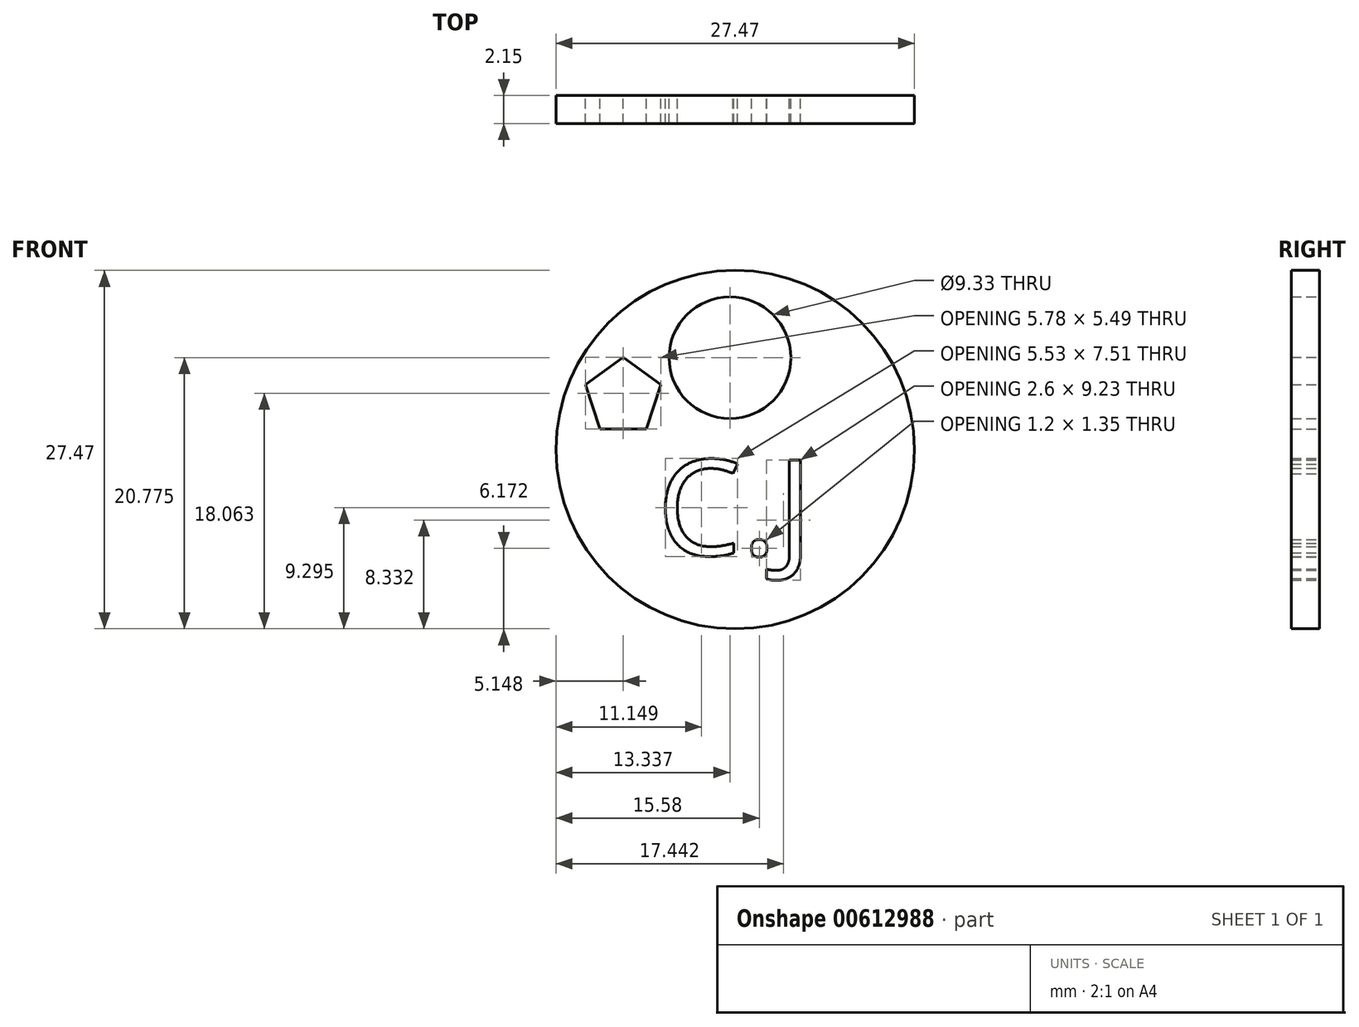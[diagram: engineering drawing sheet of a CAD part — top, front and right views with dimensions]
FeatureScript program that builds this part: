
annotation { "Feature Type Name" : "Feature", "Feature Type Description" : "" }
export const myFeature = defineFeature(function(context is Context, id is Id, definition is map)
    precondition{}
    {
        {
            var Q0;
            Q0=qCreatedBy(makeId("Front.planeOp"),FACE);
            var sketch = newSketch(context, id + "F0", { "sketchPlane" : qUnion([Q0])});
            skCircle(sketch, "E0", {"center": v(-26.62, 21.08) * mm, "radius": 13.74 * mm});
            skPoint(sketch, "E1", {"position": v(-27.64, 34.78) * mm});
            skPoint(sketch, "E2", {"position": v(-27.64, 7.38) * mm});
            skSolve(sketch);
        }
        {
            var Q0;
            Q0 = qSketchRegion(id + "F0", true);
            extrude(context, id + "F1", {"entities" : qUnion([Q0]), "depth" : 2.15 * mm, "offsetDistance" : 25 * mm});
        }
        {
            var Q0;
            Q0=qCreatedBy(makeId("Front.planeOp"),FACE);
            var sketch = newSketch(context, id + "F2", { "sketchPlane" : qUnion([Q0])});
            skCircle(sketch, "E3", {"center": v(-27.02, 28.12) * mm, "radius": 4.66 * mm});
            skSolve(sketch);
        }
        {
            var Q0;
            Q0=makeQuery(id+"F2.imprint","IMPRINT",FACE,{"disambiguationData":[TD([[makeQuery(id+"F2.imprint","IMPRINT",EDGE,{"derivedFrom":sQuery(id+"F2.wireOp",EDGE,"E3")}),1.0]])]});
            extrude(context, id + "F3", {"entities" : qUnion([Q0]), "operationType" : NewBodyOperationType.REMOVE, "endBound" : BoundingType.UP_TO_NEXT, "depth" : 25 * mm, "offsetDistance" : 25 * mm});
        }
        {
            var Q0;
            Q0=qCreatedBy(makeId("Front.planeOp"),FACE);
            var sketch = newSketch(context, id + "F4", { "sketchPlane" : qUnion([Q0])});
            skText(sketch, "E4", { "text": "C.J", "fontName": "OpenSans-Regular.ttf"});
            const initialGuessF4  = {"E4": [-0.0326, 0.01298, 1, 0, 0.00737]};
            skSetInitialGuess(sketch, initialGuessF4);
            skSolve(sketch);
        }
        {
            var Q0;
            Q0 = qSketchRegion(id + "F4", true);
            extrude(context, id + "F5", {"entities" : qUnion([Q0]), "operationType" : NewBodyOperationType.REMOVE, "endBound" : BoundingType.UP_TO_NEXT, "depth" : 25 * mm, "offsetDistance" : 25 * mm});
        }
        {
            var Q0;
            Q0=qCreatedBy(makeId("Front.planeOp"),FACE);
            var sketch = newSketch(context, id + "F6", { "sketchPlane" : qUnion([Q0])});
            skCircle(sketch, "E5.cCircle", {"center": v(-35.21, 25.11) * mm, "radius": 2.46 * mm, "construction": true});
            skLineSegment(sketch, "E5.0", {"start": v(-33.43, 22.66) * mm, "end": v(-37, 22.66) * mm});
            skLineSegment(sketch, "E5.1", {"start": v(-37, 22.66) * mm, "end": v(-38.1, 26.05) * mm});
            skLineSegment(sketch, "E5.2", {"start": v(-38.1, 26.05) * mm, "end": v(-35.21, 28.15) * mm});
            skLineSegment(sketch, "E5.3", {"start": v(-35.21, 28.15) * mm, "end": v(-32.32, 26.05) * mm});
            skLineSegment(sketch, "E5.4", {"start": v(-32.32, 26.05) * mm, "end": v(-33.43, 22.66) * mm});
            skPoint(sketch, "E5.0.midPoint", {"position": v(-35.21, 22.66) * mm});
            skSolve(sketch);
        }
        {
            var Q0;
            Q0 = qSketchRegion(id + "F6", true);
            extrude(context, id + "F7", {"entities" : qUnion([Q0]), "operationType" : NewBodyOperationType.REMOVE, "endBound" : BoundingType.UP_TO_NEXT, "depth" : 25 * mm, "offsetDistance" : 25 * mm});
        }
    });
